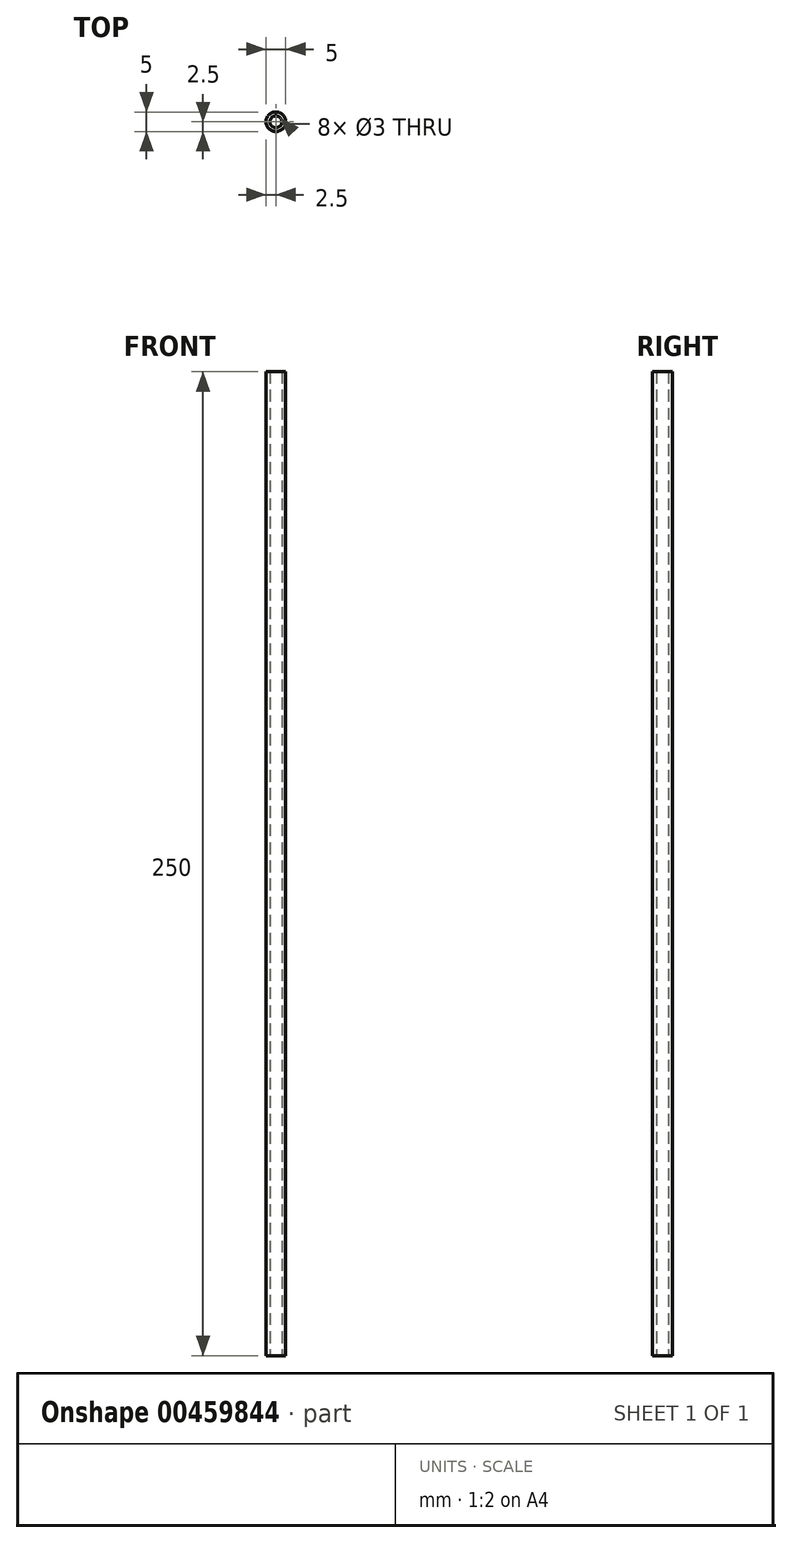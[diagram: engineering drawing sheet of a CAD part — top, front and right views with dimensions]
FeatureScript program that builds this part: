
annotation { "Feature Type Name" : "Feature", "Feature Type Description" : "" }
export const myFeature = defineFeature(function(context is Context, id is Id, definition is map)
    precondition{}
    {
        {
            var Q0;
            Q0=qCreatedBy(makeId("Top.planeOp"),FACE);
            var sketch = newSketch(context, id + "F0", { "sketchPlane" : qUnion([Q0])});
            skCircle(sketch, "E0", {"center": v(0, 0) * mm, "radius": 1.5 * mm});
            skCircle(sketch, "E1", {"center": v(0, 0) * mm, "radius": 2.5 * mm});
            skSolve(sketch);
        }
        {
            var Q0;
            Q0=qSketchRegion(id+"F0",true);
            extrude(context, id + "F1", {"entities" : qUnion([Q0]), "depth" : 250 * mm, "offsetDistance" : 25 * mm});
        }
    });
